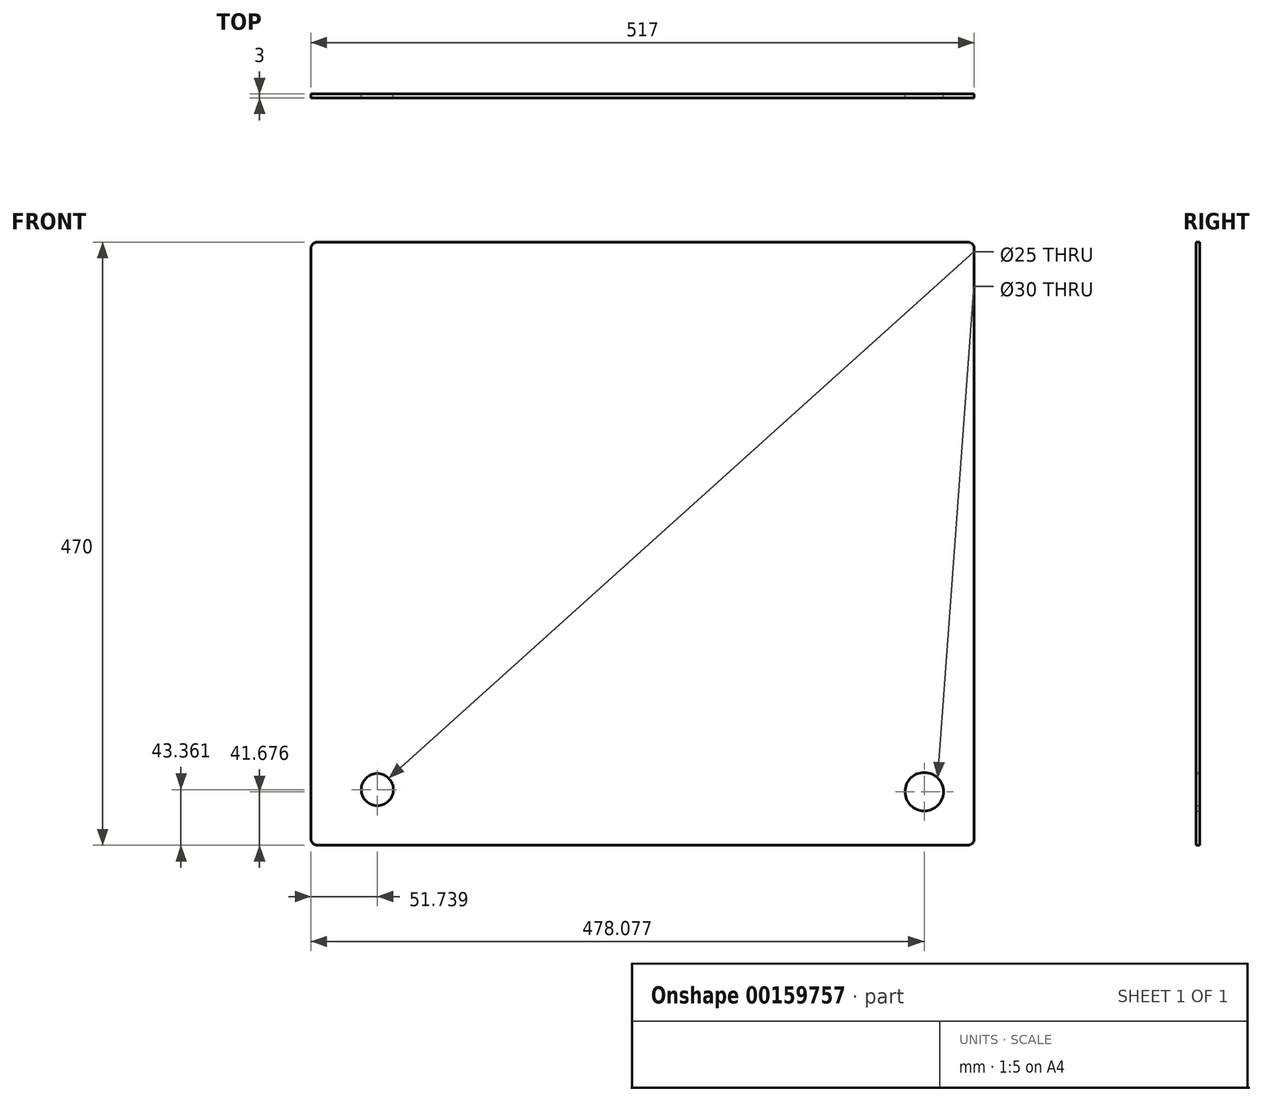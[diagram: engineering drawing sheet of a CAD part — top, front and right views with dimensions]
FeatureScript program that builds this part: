
annotation { "Feature Type Name" : "Feature", "Feature Type Description" : "" }
export const myFeature = defineFeature(function(context is Context, id is Id, definition is map)
    precondition{}
    {
        {
            var Q0;
            Q0=qCreatedBy(makeId("Front.planeOp"),FACE);
            var sketch = newSketch(context, id + "F0", { "sketchPlane" : qUnion([Q0])});
            skLineSegment(sketch, "E0.bottom", {"start": v(-439.16, 401.14) * mm, "end": v(67.84, 401.14) * mm});
            skLineSegment(sketch, "E0.top", {"start": v(-439.16, -68.86) * mm, "end": v(67.84, -68.86) * mm});
            skLineSegment(sketch, "E0.left", {"start": v(-444.16, 396.14) * mm, "end": v(-444.16, -63.86) * mm});
            skLineSegment(sketch, "E0.right", {"start": v(72.84, 396.14) * mm, "end": v(72.84, -63.86) * mm});
            skPoint(sketch, "E1.visualSharp", {"position": v(-444.16, 401.14) * mm});
            skArc(sketch, "E1.filletArc", {"start": v(-439.16, 401.14) * mm, "mid": v(-442.7, 399.67) * mm, "end": v(-444.16, 396.14) * mm});
            skPoint(sketch, "E2.visualSharp", {"position": v(72.84, 401.14) * mm});
            skArc(sketch, "E2.filletArc", {"start": v(72.84, 396.14) * mm, "mid": v(71.38, 399.67) * mm, "end": v(67.84, 401.14) * mm});
            skPoint(sketch, "E3.visualSharp", {"position": v(72.84, -68.86) * mm});
            skArc(sketch, "E3.filletArc", {"start": v(67.84, -68.86) * mm, "mid": v(71.38, -67.4) * mm, "end": v(72.84, -63.86) * mm});
            skPoint(sketch, "E4.visualSharp", {"position": v(-444.16, -68.86) * mm});
            skArc(sketch, "E4.filletArc", {"start": v(-444.16, -63.86) * mm, "mid": v(-442.7, -67.4) * mm, "end": v(-439.16, -68.86) * mm});
            skCircle(sketch, "E5", {"center": v(-392.42, -25.5) * mm, "radius": 12.5 * mm});
            skCircle(sketch, "E6", {"center": v(33.92, -27.18) * mm, "radius": 15 * mm});
            skSolve(sketch);
        }
        {
            var Q0;
            Q0=makeQuery(id+"F0.imprint","IMPRINT",FACE,{"disambiguationData":[TD([[makeQuery(id+"F0.imprint","IMPRINT",EDGE,{"derivedFrom":sQuery(id+"F0.wireOp",EDGE,"E0.bottom")}),-1.0]])]});
            extrude(context, id + "F1", {"entities" : qUnion([Q0]), "depth" : 3 * mm});
        }
    });
